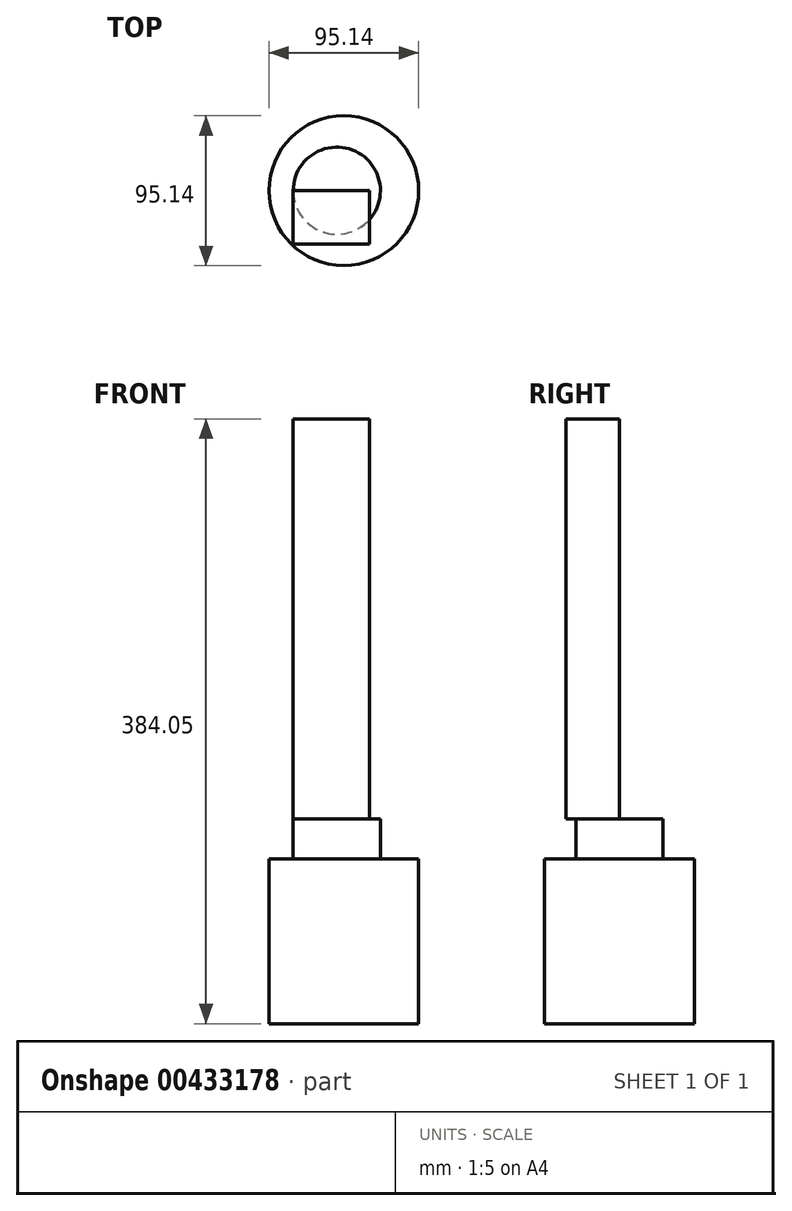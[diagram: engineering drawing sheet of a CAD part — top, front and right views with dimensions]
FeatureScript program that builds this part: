
annotation { "Feature Type Name" : "Feature", "Feature Type Description" : "" }
export const myFeature = defineFeature(function(context is Context, id is Id, definition is map)
    precondition{}
    {
        {
            var Q0;
            Q0=qCreatedBy(makeId("Top.planeOp"),FACE);
            var sketch = newSketch(context, id + "F0", { "sketchPlane" : qUnion([Q0])});
            skCircle(sketch, "E0", {"center": v(0, 0) * mm, "radius": 47.57 * mm});
            skSolve(sketch);
        }
        {
            var Q0;
            Q0=makeQuery(id+"F0.imprint","IMPRINT",FACE,{"disambiguationData":[TD([[makeQuery(id+"F0.imprint","IMPRINT",EDGE,{"derivedFrom":sQuery(id+"F0.wireOp",EDGE,"E0")}),1.0]])]});
            extrude(context, id + "F1", {"entities" : qUnion([Q0]), "depth" : 104.65 * mm});
        }
        {
            var Q0;
            Q0=makeQuery(id+"F1.opExtrude","CAP_FACE",FACE,{"disambiguationData":[OSD([sQuery(id+"F0.wireOp",EDGE,"E0")])],"isStart":false});
            var sketch = newSketch(context, id + "F2", { "sketchPlane" : qUnion([Q0])});
            skCircle(sketch, "E1", {"center": v(-4.46, 0) * mm, "radius": 27.68 * mm});
            skSolve(sketch);
        }
        {
            var Q0;
            Q0=makeQuery(id+"F2.imprint","IMPRINT",FACE,{"disambiguationData":[TD([[makeQuery(id+"F2.imprint","IMPRINT",EDGE,{"derivedFrom":sQuery(id+"F2.wireOp",EDGE,"E1")}),1.0]])]});
            extrude(context, id + "F3", {"entities" : qUnion([Q0]), "operationType" : NewBodyOperationType.ADD, "depth" : 25.4 * mm});
        }
        {
            var Q0;
            Q0=makeQuery(id+"F3.opExtrude","CAP_FACE",FACE,{"disambiguationData":[OSD([sQuery(id+"F2.wireOp",EDGE,"E1")])],"isStart":false});
            var sketch = newSketch(context, id + "F4", { "sketchPlane" : qUnion([Q0])});
            skLineSegment(sketch, "E2.bottom", {"start": v(-32.15, 0) * mm, "end": v(16.19, 0) * mm});
            skLineSegment(sketch, "E2.top", {"start": v(-32.15, -34) * mm, "end": v(16.19, -34) * mm});
            skLineSegment(sketch, "E2.left", {"start": v(-32.15, 0) * mm, "end": v(-32.15, -34) * mm});
            skLineSegment(sketch, "E2.right", {"start": v(16.19, 0) * mm, "end": v(16.19, -34) * mm});
            skSolve(sketch);
        }
        {
            var Q0;
            Q0 = qSketchRegion(id + "F4", true);
            extrude(context, id + "F5", {"entities" : qUnion([Q0]), "operationType" : NewBodyOperationType.ADD, "depth" : 254 * mm});
        }
    });
